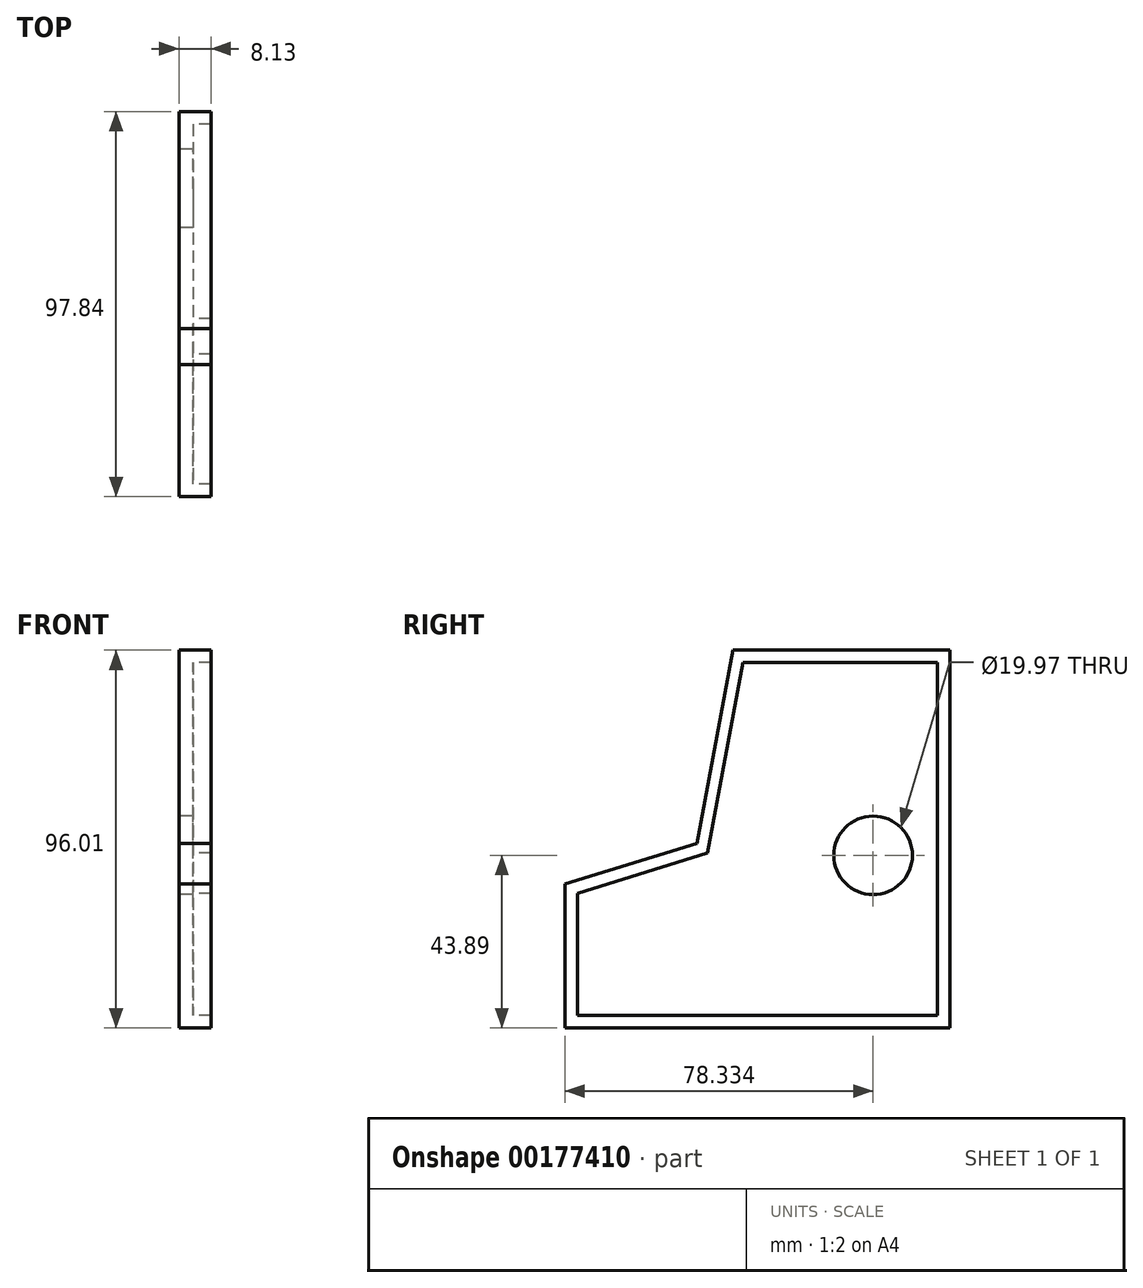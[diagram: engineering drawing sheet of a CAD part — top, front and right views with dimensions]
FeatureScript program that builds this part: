
annotation { "Feature Type Name" : "Feature", "Feature Type Description" : "" }
export const myFeature = defineFeature(function(context is Context, id is Id, definition is map)
    precondition{}
    {
        {
            var Q0;
            Q0=qCreatedBy(makeId("Right.planeOp"),FACE);
            var sketch = newSketch(context, id + "F0", { "sketchPlane" : qUnion([Q0])});
            skLineSegment(sketch, "E0", {"start": v(44.5, 64.16) * mm, "end": v(44.5, -31.85) * mm});
            skLineSegment(sketch, "E1", {"start": v(44.5, -31.85) * mm, "end": v(-53.34, -31.85) * mm});
            skLineSegment(sketch, "E2", {"start": v(-53.34, -31.85) * mm, "end": v(-53.34, 4.72) * mm});
            skLineSegment(sketch, "E3", {"start": v(-53.34, 4.72) * mm, "end": v(-19.81, 15.09) * mm});
            skLineSegment(sketch, "E4", {"start": v(-19.81, 15.09) * mm, "end": v(-10.67, 64.16) * mm});
            skLineSegment(sketch, "E5", {"start": v(44.5, 64.16) * mm, "end": v(-10.67, 64.16) * mm});
            skSolve(sketch);
        }
        {
            var Q0;
            Q0 = qSketchRegion(id + "F0", true);
            extrude(context, id + "F1", {"entities" : qUnion([Q0]), "depth" : 3.56 * mm});
        }
        {
            var Q0;
            Q0=makeQuery(id+"F1.opExtrude","CAP_FACE",FACE,{"disambiguationData":[OSD([sQuery(id+"F0.wireOp",EDGE,"E0"),sQuery(id+"F0.wireOp",EDGE,"E1"),sQuery(id+"F0.wireOp",EDGE,"E2"),sQuery(id+"F0.wireOp",EDGE,"E3"),sQuery(id+"F0.wireOp",EDGE,"E4"),sQuery(id+"F0.wireOp",EDGE,"E5")])],"isStart":false});
            var sketch = newSketch(context, id + "F2", { "sketchPlane" : qUnion([Q0])});
            skLineSegment(sketch, "E6.0", {"start": v(-19.81, 15.09) * mm, "end": v(-10.67, 64.16) * mm});
            skLineSegment(sketch, "E7.0", {"start": v(-53.34, 4.72) * mm, "end": v(-19.81, 15.09) * mm});
            skLineSegment(sketch, "E8.0", {"start": v(-53.34, -31.85) * mm, "end": v(-53.34, 4.72) * mm});
            skLineSegment(sketch, "E9.0", {"start": v(44.5, -31.85) * mm, "end": v(-53.34, -31.85) * mm});
            skLineSegment(sketch, "E10.0", {"start": v(44.5, 64.16) * mm, "end": v(44.5, -31.85) * mm});
            skLineSegment(sketch, "E11.0", {"start": v(41.33, 60.99) * mm, "end": v(41.33, -28.68) * mm});
            skLineSegment(sketch, "E11.1", {"start": v(-17.04, 12.62) * mm, "end": v(-8.03, 60.99) * mm});
            skLineSegment(sketch, "E11.2", {"start": v(-50.17, 2.38) * mm, "end": v(-17.04, 12.62) * mm});
            skLineSegment(sketch, "E11.3", {"start": v(41.33, 60.99) * mm, "end": v(-8.03, 60.99) * mm});
            skLineSegment(sketch, "E11.4", {"start": v(-50.17, -28.68) * mm, "end": v(-50.17, 2.38) * mm});
            skLineSegment(sketch, "E11.5", {"start": v(41.33, -28.68) * mm, "end": v(-50.17, -28.68) * mm});
            skSolve(sketch);
        }
        {
            var Q0;
            Q0=makeQuery(id+"F2.imprint","IMPRINT",FACE,{"disambiguationData":[TD([[makeQuery(id+"F2.imprint","IMPRINT",EDGE,{"derivedFrom":sQuery(id+"F2.wireOp",EDGE,"E6.0")}),-1.0]])]});
            extrude(context, id + "F3", {"entities" : qUnion([Q0]), "operationType" : NewBodyOperationType.ADD, "depth" : 4.57 * mm});
        }
        {
            var Q0;
            Q0=makeQuery(id+"F1.opExtrude","CAP_FACE",FACE,{"disambiguationData":[OSD([sQuery(id+"F0.wireOp",EDGE,"E0"),sQuery(id+"F0.wireOp",EDGE,"E1"),sQuery(id+"F0.wireOp",EDGE,"E2"),sQuery(id+"F0.wireOp",EDGE,"E3"),sQuery(id+"F0.wireOp",EDGE,"E4"),sQuery(id+"F0.wireOp",EDGE,"E5")])],"isStart":true});
            var sketch = newSketch(context, id + "F4", { "sketchPlane" : qUnion([Q0])});
            skCircle(sketch, "E12", {"center": v(-25, 12.04) * mm, "radius": 9.98 * mm});
            skSolve(sketch);
        }
        {
            var Q0;
            Q0 = qSketchRegion(id + "F4", true);
            extrude(context, id + "F5", {"entities" : qUnion([Q0]), "operationType" : NewBodyOperationType.REMOVE, "oppositeDirection" : true, "depth" : 25.4 * mm});
        }
    });
